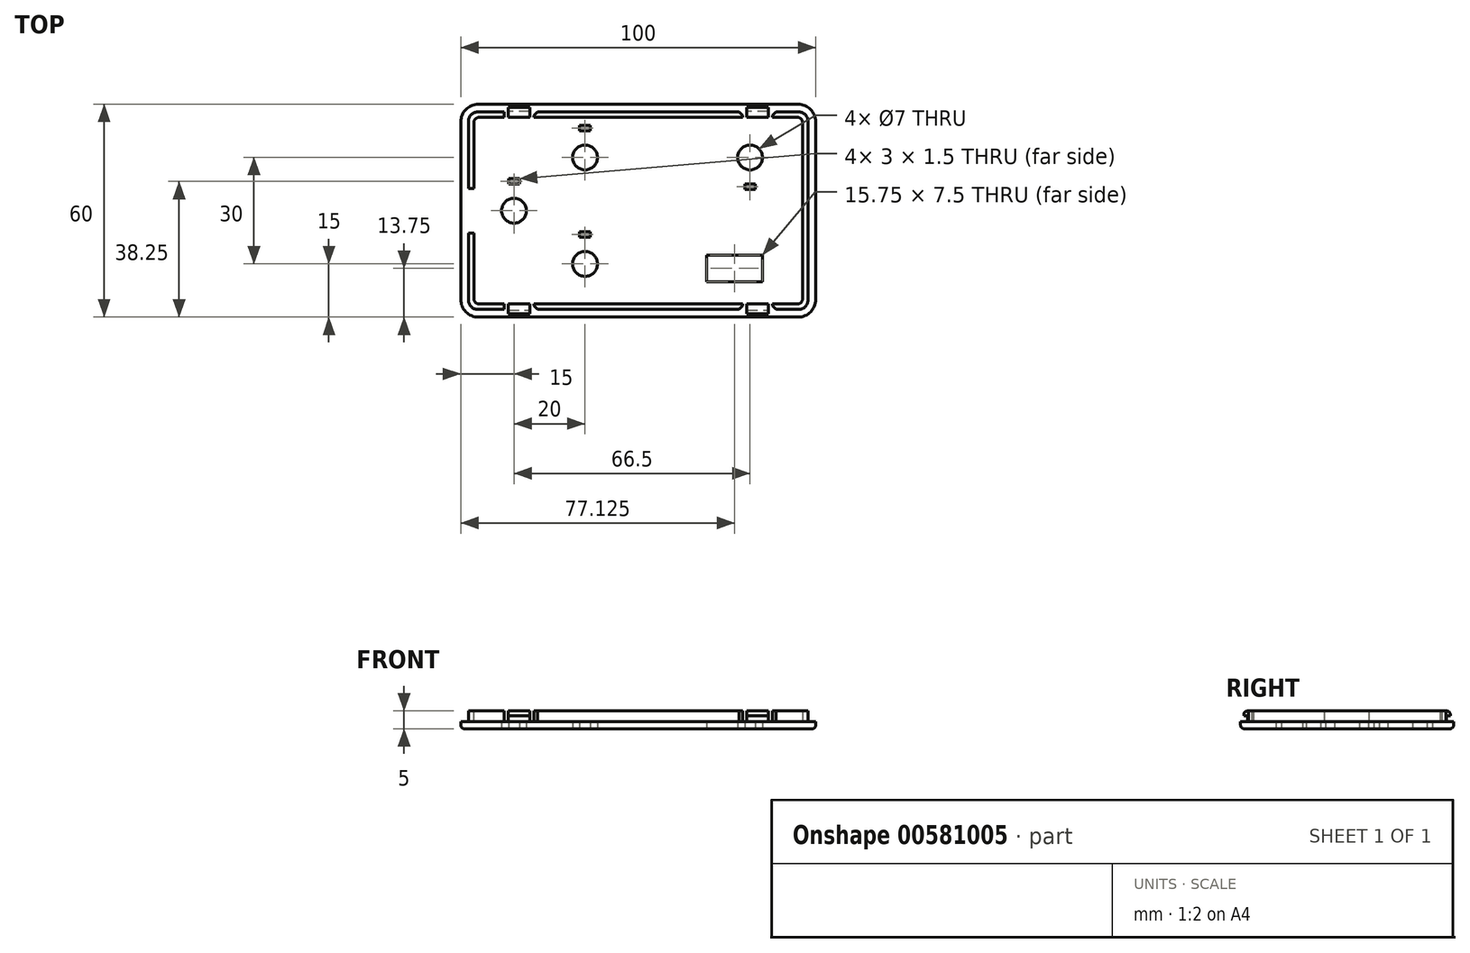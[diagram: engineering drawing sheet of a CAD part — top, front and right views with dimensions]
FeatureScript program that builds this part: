
annotation { "Feature Type Name" : "Feature", "Feature Type Description" : "" }
export const myFeature = defineFeature(function(context is Context, id is Id, definition is map)
    precondition{}
    {
        {
            var Q0;
            Q0=qCreatedBy(makeId("Top.planeOp"),FACE);
            var sketch = newSketch(context, id + "F0", { "sketchPlane" : qUnion([Q0])});
            skLineSegment(sketch, "E0.bottom", {"start": v(5, 0) * mm, "end": v(95, 0) * mm});
            skLineSegment(sketch, "E0.left", {"start": v(0, 5) * mm, "end": v(0, 30) * mm});
            skLineSegment(sketch, "E0.right", {"start": v(100, 5) * mm, "end": v(100, 30) * mm});
            skLineSegment(sketch, "E1.top", {"start": v(4.7, 2.2) * mm, "end": v(95.3, 2.2) * mm});
            skLineSegment(sketch, "E1.left", {"start": v(2.2, 30) * mm, "end": v(2.2, 4.7) * mm});
            skLineSegment(sketch, "E1.right", {"start": v(97.8, 30) * mm, "end": v(97.8, 4.7) * mm});
            skPoint(sketch, "E2.visualSharp", {"position": v(0, 0) * mm});
            skArc(sketch, "E2.filletArc", {"start": v(0, 5) * mm, "mid": v(1.46, 1.46) * mm, "end": v(5, 0) * mm});
            skPoint(sketch, "E3.visualSharp", {"position": v(100, 0) * mm});
            skArc(sketch, "E3.filletArc", {"start": v(95, 0) * mm, "mid": v(98.54, 1.46) * mm, "end": v(100, 5) * mm});
            skPoint(sketch, "E4.visualSharp", {"position": v(97.8, 2.2) * mm});
            skArc(sketch, "E4.filletArc", {"start": v(95.3, 2.2) * mm, "mid": v(97.07, 2.93) * mm, "end": v(97.8, 4.7) * mm});
            skPoint(sketch, "E5.visualSharp", {"position": v(2.2, 2.2) * mm});
            skArc(sketch, "E5.filletArc", {"start": v(2.2, 4.7) * mm, "mid": v(2.93, 2.93) * mm, "end": v(4.7, 2.2) * mm});
            skLineSegment(sketch, "E6.1", {"start": v(3.7, 30) * mm, "end": v(3.7, 5.2) * mm});
            skLineSegment(sketch, "E6.2", {"start": v(5.2, 3.7) * mm, "end": v(94.8, 3.7) * mm});
            skLineSegment(sketch, "E6.3", {"start": v(96.3, 30) * mm, "end": v(96.3, 5.2) * mm});
            skPoint(sketch, "E7.visualSharp", {"position": v(96.3, 3.7) * mm});
            skArc(sketch, "E7.filletArc", {"start": v(94.8, 3.7) * mm, "mid": v(95.86, 4.14) * mm, "end": v(96.3, 5.2) * mm});
            skPoint(sketch, "E8.visualSharp", {"position": v(3.7, 3.7) * mm});
            skArc(sketch, "E8.filletArc", {"start": v(3.7, 5.2) * mm, "mid": v(4.14, 4.14) * mm, "end": v(5.2, 3.7) * mm});
            skLineSegment(sketch, "E9", {"start": v(0, 30) * mm, "end": v(100, 30) * mm});
            skSolve(sketch);
        }
        {
            var Q0;
            Q0=qSketchRegion(id+"F0",true);
            var Q1;
            Q1=makeQuery(id+"F0.imprint","IMPRINT",FACE,{"disambiguationData":[TD([[makeQuery(id+"F0.imprint","IMPRINT",EDGE,{"derivedFrom":sQuery(id+"F0.wireOp",EDGE,"E6.0")}),-1.0]])]});
            var Q2;
            Q2=makeQuery(id+"F0.imprint","IMPRINT",FACE,{"disambiguationData":[TD([[makeQuery(id+"F0.imprint","IMPRINT",EDGE,{"derivedFrom":sQuery(id+"F0.wireOp",EDGE,"E1.bottom")}),-1.0]])]});
            extrude(context, id + "F1", {"entities" : qUnion([Q0, Q1, Q2]), "depth" : 2 * mm, "offsetDistance" : 25 * mm});
        }
        {
            var Q0;
            Q0=makeQuery(id+"F0.imprint","IMPRINT",FACE,{"disambiguationData":[TD([[makeQuery(id+"F0.imprint","IMPRINT",EDGE,{"derivedFrom":sQuery(id+"F0.wireOp",EDGE,"E1.top")}),1.0]])]});
            extrude(context, id + "F2", {"entities" : qUnion([Q0]), "operationType" : NewBodyOperationType.ADD, "depth" : 5 * mm, "offsetDistance" : 25 * mm});
        }
        {
            var Q0;
            Q0=makeQuery(id+"F2.opExtrude","CAP_FACE",FACE,{"disambiguationData":[OSD([sQuery(id+"F0.wireOp",EDGE,"E1.top"),sQuery(id+"F0.wireOp",EDGE,"E1.left"),sQuery(id+"F0.wireOp",EDGE,"E1.right"),sQuery(id+"F0.wireOp",EDGE,"E4.filletArc"),sQuery(id+"F0.wireOp",EDGE,"E5.filletArc"),sQuery(id+"F0.wireOp",EDGE,"E6.1"),sQuery(id+"F0.wireOp",EDGE,"E6.2"),sQuery(id+"F0.wireOp",EDGE,"E6.3"),sQuery(id+"F0.wireOp",EDGE,"E7.filletArc"),sQuery(id+"F0.wireOp",EDGE,"E8.filletArc"),sQuery(id+"F0.wireOp",EDGE,"E9")])],"isStart":false});
            var sketch = newSketch(context, id + "F3", { "sketchPlane" : qUnion([Q0])});
            skLineSegment(sketch, "E10.bottom", {"start": v(2.2, 30) * mm, "end": v(3.7, 30) * mm});
            skLineSegment(sketch, "E10.top", {"start": v(2.2, 23.7) * mm, "end": v(3.7, 23.7) * mm});
            skLineSegment(sketch, "E10.left", {"start": v(2.2, 30) * mm, "end": v(2.2, 23.7) * mm});
            skLineSegment(sketch, "E10.right", {"start": v(3.7, 30) * mm, "end": v(3.7, 23.7) * mm});
            skLineSegment(sketch, "E11.bottom", {"start": v(12.2, 3.7) * mm, "end": v(13.4, 3.7) * mm});
            skLineSegment(sketch, "E11.top", {"start": v(12.2, 2.2) * mm, "end": v(13.4, 2.2) * mm});
            skLineSegment(sketch, "E11.left", {"start": v(12.2, 3.7) * mm, "end": v(12.2, 2.2) * mm});
            skLineSegment(sketch, "E11.right", {"start": v(13.4, 3.7) * mm, "end": v(13.4, 2.2) * mm});
            skLineSegment(sketch, "E12.bottom", {"start": v(86.6, 3.7) * mm, "end": v(87.8, 3.7) * mm});
            skLineSegment(sketch, "E12.top", {"start": v(86.6, 2.2) * mm, "end": v(87.8, 2.2) * mm});
            skLineSegment(sketch, "E12.left", {"start": v(86.6, 3.7) * mm, "end": v(86.6, 2.2) * mm});
            skLineSegment(sketch, "E12.right", {"start": v(87.8, 3.7) * mm, "end": v(87.8, 2.2) * mm});
            skLineSegment(sketch, "E13.bottom", {"start": v(19.4, 3.7) * mm, "end": v(20.6, 3.7) * mm});
            skLineSegment(sketch, "E13.top", {"start": v(19.4, 2.2) * mm, "end": v(20.6, 2.2) * mm});
            skLineSegment(sketch, "E13.left", {"start": v(19.4, 3.7) * mm, "end": v(19.4, 2.2) * mm});
            skLineSegment(sketch, "E13.right", {"start": v(20.6, 3.7) * mm, "end": v(20.6, 2.2) * mm});
            skLineSegment(sketch, "E14.bottom", {"start": v(80.6, 3.7) * mm, "end": v(79.4, 3.7) * mm});
            skLineSegment(sketch, "E14.top", {"start": v(80.6, 2.2) * mm, "end": v(79.4, 2.2) * mm});
            skLineSegment(sketch, "E14.left", {"start": v(80.6, 3.7) * mm, "end": v(80.6, 2.2) * mm});
            skLineSegment(sketch, "E14.right", {"start": v(79.4, 3.7) * mm, "end": v(79.4, 2.2) * mm});
            skSolve(sketch);
        }
        {
            var Q0;
            Q0=makeQuery(id+"F3.imprint","IMPRINT",FACE,{"disambiguationData":[TD([[makeQuery(id+"F3.imprint","IMPRINT",EDGE,{"derivedFrom":sQuery(id+"F3.wireOp",EDGE,"E10.bottom")}),-1.0]])]});
            var Q1;
            Q1=makeQuery(id+"F3.imprint","IMPRINT",FACE,{"disambiguationData":[TD([[makeQuery(id+"F3.imprint","IMPRINT",EDGE,{"derivedFrom":sQuery(id+"F3.wireOp",EDGE,"E11.bottom")}),-1.0]])]});
            var Q2;
            Q2=makeQuery(id+"F3.imprint","IMPRINT",FACE,{"disambiguationData":[TD([[makeQuery(id+"F3.imprint","IMPRINT",EDGE,{"derivedFrom":sQuery(id+"F3.wireOp",EDGE,"E13.bottom")}),-1.0]])]});
            var Q3;
            Q3=makeQuery(id+"F3.imprint","IMPRINT",FACE,{"disambiguationData":[TD([[makeQuery(id+"F3.imprint","IMPRINT",EDGE,{"derivedFrom":sQuery(id+"F3.wireOp",EDGE,"E14.bottom")}),-1.0]])]});
            var Q4;
            Q4=makeQuery(id+"F3.imprint","IMPRINT",FACE,{"disambiguationData":[TD([[makeQuery(id+"F3.imprint","IMPRINT",EDGE,{"derivedFrom":sQuery(id+"F3.wireOp",EDGE,"E12.bottom")}),-1.0]])]});
            extrude(context, id + "F4", {"entities" : qUnion([Q0, Q1, Q2, Q3, Q4]), "operationType" : NewBodyOperationType.REMOVE, "oppositeDirection" : true, "depth" : 3 * mm, "offsetDistance" : 25 * mm});
        }
        {
            var Q0;
            {var subQ0=sQuery(id+"F3.wireOp",EDGE,"E11.right");var subQ2=sQuery(id+"F0.wireOp",EDGE,"E1.top");Q0=makeQuery(id+"F4.boolean.opBoolean","SPLIT",FACE,{"disambiguationData":[TD([makeQuery(id+"F4.opExtrude","SWEPT_FACE",FACE,{"disambiguationData":[OSD([subQ0])]})])],"derivedFrom":makeQuery(id+"F2.opExtrude","SWEPT_FACE",FACE,{"disambiguationData":[OSD([subQ2])]})});}
            var Q1;
            {var subQ1=sQuery(id+"F0.wireOp",EDGE,"E1.top");var subQ3=sQuery(id+"F3.wireOp",EDGE,"E12.left");Q1=makeQuery(id+"F4.boolean.opBoolean","SPLIT",FACE,{"disambiguationData":[TD([makeQuery(id+"F4.opExtrude","SWEPT_FACE",FACE,{"disambiguationData":[OSD([subQ3])]})])],"derivedFrom":makeQuery(id+"F2.opExtrude","SWEPT_FACE",FACE,{"disambiguationData":[OSD([subQ1])]})});}
            extrude(context, id + "F5", {"entities" : qUnion([Q0, Q1]), "operationType" : NewBodyOperationType.ADD, "depth" : 0.2 * mm, "offsetDistance" : 25 * mm});
        }
        {
            var Q0;
            {var subQ0=sQuery(id+"F3.wireOp",EDGE,"E11.right");var subQ2=sQuery(id+"F0.wireOp",EDGE,"E1.top");Q0=makeQuery(id+"F5.opExtrude","CAP_FACE",FACE,{"disambiguationData":[OSD([subQ2]),TDD([makeQuery(id+"F4.boolean.opBoolean","SPLIT",FACE,{"disambiguationData":[TD([makeQuery(id+"F4.opExtrude","SWEPT_FACE",FACE,{"disambiguationData":[OSD([subQ0])]})])],"derivedFrom":makeQuery(id+"F2.opExtrude","SWEPT_FACE",FACE,{"disambiguationData":[OSD([subQ2])]})})])],"isStart":false});}
            var sketch = newSketch(context, id + "F6", { "sketchPlane" : qUnion([Q0])});
            skLineSegment(sketch, "E15.bottom", {"start": v(13.4, 5) * mm, "end": v(19.4, 5) * mm});
            skLineSegment(sketch, "E15.top", {"start": v(13.4, 3.7) * mm, "end": v(19.4, 3.7) * mm});
            skLineSegment(sketch, "E15.left", {"start": v(13.4, 5) * mm, "end": v(13.4, 3.7) * mm});
            skLineSegment(sketch, "E15.right", {"start": v(19.4, 5) * mm, "end": v(19.4, 3.7) * mm});
            skSolve(sketch);
        }
        {
            var Q0;
            {var subQ1=sQuery(id+"F0.wireOp",EDGE,"E1.top");var subQ3=sQuery(id+"F3.wireOp",EDGE,"E12.left");Q0=makeQuery(id+"F5.opExtrude","CAP_FACE",FACE,{"disambiguationData":[OSD([subQ1]),TDD([makeQuery(id+"F4.boolean.opBoolean","SPLIT",FACE,{"disambiguationData":[TD([makeQuery(id+"F4.opExtrude","SWEPT_FACE",FACE,{"disambiguationData":[OSD([subQ3])]})])],"derivedFrom":makeQuery(id+"F2.opExtrude","SWEPT_FACE",FACE,{"disambiguationData":[OSD([subQ1])]})})])],"isStart":false});}
            var sketch = newSketch(context, id + "F7", { "sketchPlane" : qUnion([Q0])});
            skLineSegment(sketch, "E16.bottom", {"start": v(80.6, 5) * mm, "end": v(86.6, 5) * mm});
            skLineSegment(sketch, "E16.top", {"start": v(80.6, 3.7) * mm, "end": v(86.6, 3.7) * mm});
            skLineSegment(sketch, "E16.left", {"start": v(80.6, 5) * mm, "end": v(80.6, 3.7) * mm});
            skLineSegment(sketch, "E16.right", {"start": v(86.6, 5) * mm, "end": v(86.6, 3.7) * mm});
            skSolve(sketch);
        }
        {
            var Q0;
            Q0=makeQuery(id+"F6.imprint","IMPRINT",FACE,{"disambiguationData":[TD([[makeQuery(id+"F6.imprint","IMPRINT",EDGE,{"derivedFrom":sQuery(id+"F6.wireOp",EDGE,"E15.bottom")}),-1.0]])]});
            var Q1;
            Q1=makeQuery(id+"F7.imprint","IMPRINT",FACE,{"disambiguationData":[TD([[makeQuery(id+"F7.imprint","IMPRINT",EDGE,{"derivedFrom":sQuery(id+"F7.wireOp",EDGE,"E16.bottom")}),-1.0]])]});
            extrude(context, id + "F8", {"entities" : qUnion([Q0, Q1]), "operationType" : NewBodyOperationType.ADD, "depth" : 1.1 * mm, "offsetDistance" : 25 * mm});
        }
        {
            var Q0;
            Q0=makeQuery(id+"F8.opExtrude","CAP_EDGE",EDGE,{"disambiguationData":[OSD([sQuery(id+"F6.wireOp",EDGE,"E15.bottom")])],"isStart":false});
            var Q1;
            Q1=makeQuery(id+"F8.opExtrude","CAP_EDGE",EDGE,{"disambiguationData":[OSD([sQuery(id+"F7.wireOp",EDGE,"E16.bottom")])],"isStart":false});
            fillet(context, id + "F9", {"entities" : qUnion([Q0, Q1]), "radius" : 1 * mm, "tangentPropagation" : true, "allowEdgeOverflow" : false});
        }
        {
            var Q0;
            Q0=makeQuery(id+"F4.boolean.opBoolean","COPY",EDGE,{"derivedFrom":makeQuery(id+"F4.opExtrude","SWEPT_EDGE",EDGE,{"disambiguationData":[OSD([sQuery(id+"F0.wireOp",EDGE,"E1.top"),sQuery(id+"F3.wireOp",EDGE,"E13.top"),sQuery(id+"F3.wireOp",EDGE,"E13.right")])]})});
            var Q1;
            Q1=makeQuery(id+"F4.boolean.opBoolean","COPY",EDGE,{"derivedFrom":makeQuery(id+"F4.opExtrude","SWEPT_EDGE",EDGE,{"disambiguationData":[OSD([sQuery(id+"F0.wireOp",EDGE,"E1.top"),sQuery(id+"F3.wireOp",EDGE,"E11.top"),sQuery(id+"F3.wireOp",EDGE,"E11.left")])]})});
            var Q2;
            Q2=makeQuery(id+"F4.boolean.opBoolean","COPY",EDGE,{"derivedFrom":makeQuery(id+"F4.opExtrude","SWEPT_EDGE",EDGE,{"disambiguationData":[OSD([sQuery(id+"F0.wireOp",EDGE,"E1.top"),sQuery(id+"F3.wireOp",EDGE,"E14.top"),sQuery(id+"F3.wireOp",EDGE,"E14.right")])]})});
            var Q3;
            Q3=makeQuery(id+"F4.boolean.opBoolean","COPY",EDGE,{"derivedFrom":makeQuery(id+"F4.opExtrude","SWEPT_EDGE",EDGE,{"disambiguationData":[OSD([sQuery(id+"F0.wireOp",EDGE,"E1.top"),sQuery(id+"F3.wireOp",EDGE,"E12.top"),sQuery(id+"F3.wireOp",EDGE,"E12.right")])]})});
            var Q4;
            Q4=makeQuery(id+"F4.boolean.opBoolean","COPY",EDGE,{"derivedFrom":makeQuery(id+"F4.opExtrude","SWEPT_EDGE",EDGE,{"disambiguationData":[OSD([sQuery(id+"F0.wireOp",EDGE,"E1.left"),sQuery(id+"F3.wireOp",EDGE,"E10.top"),sQuery(id+"F3.wireOp",EDGE,"E10.left")])]})});
            chamfer(context, id + "F10", {"entities" : qUnion([Q0, Q1, Q2, Q3, Q4]), "width" : 1 * mm, "tangentPropagation" : true});
        }
        {
            var Q0;
            Q0=makeQuery(id+"F1.opExtrude","CAP_EDGE",EDGE,{"disambiguationData":[OSD([sQuery(id+"F0.wireOp",EDGE,"E0.bottom")])],"isStart":true});
            fillet(context, id + "F11", {"entities" : qUnion([Q0]), "radius" : 1 * mm, "tangentPropagation" : true, "allowEdgeOverflow" : false});
        }
        {
            var Q0;
            Q0=makeQuery(id+"F1.opExtrude","SWEPT_BODY",BODY,{"disambiguationData":[OSD([sQuery(id+"F0.wireOp",EDGE,"E0.bottom"),sQuery(id+"F0.wireOp",EDGE,"E0.left"),sQuery(id+"F0.wireOp",EDGE,"E0.right"),sQuery(id+"F0.wireOp",EDGE,"E2.filletArc"),sQuery(id+"F0.wireOp",EDGE,"E3.filletArc"),sQuery(id+"F0.wireOp",EDGE,"E9")])]});
            var Q1;
            {var subQ0=sQuery(id+"F0.wireOp",EDGE,"E0.left");var subQ1=sQuery(id+"F0.wireOp",EDGE,"E9");Q1=makeQuery(id+"FwHGnBZO1ZIo1Mn_1.boolean.opBoolean","SPLIT",FACE,{"disambiguationData":[TD([makeQuery(id+"F1.opExtrude","SWEPT_FACE",FACE,{"disambiguationData":[OSD([subQ0])]})])],"derivedFrom":makeQuery(id+"F2.boolean.opBoolean","MERGE",FACE,{"derivedFrom":[makeQuery(id+"F1.opExtrude","SWEPT_FACE",FACE,{"disambiguationData":[OSD([subQ1])]}),makeQuery(id+"F2.opExtrude","SWEPT_FACE",FACE,{"disambiguationData":[OSD([subQ1]),TDD([makeQuery(id+"F0.imprint","IMPRINT",EDGE,{"disambiguationData":[TD([[makeQuery(id+"F0.imprint","INTERSECT",VERTEX,{"derivedFrom":[sQuery(id+"F0.wireOp",EDGE,"E1.left"),subQ1]}),-1.0]])],"derivedFrom":subQ1})])]}),makeQuery(id+"F2.opExtrude","SWEPT_FACE",FACE,{"disambiguationData":[OSD([subQ1]),TDD([makeQuery(id+"F0.imprint","IMPRINT",EDGE,{"disambiguationData":[TD([[makeQuery(id+"F0.imprint","INTERSECT",VERTEX,{"derivedFrom":[sQuery(id+"F0.wireOp",EDGE,"E1.right"),subQ1]}),1.0]])],"derivedFrom":subQ1})])]})]})});}
            mirror(context, id + "F12", {"operationType" : NewBodyOperationType.ADD, "entities" : qUnion([Q0]), "mirrorPlane" : qUnion([Q1])});
        }
        {
            var Q0;
            Q0=qCreatedBy(makeId("Top.planeOp"),FACE);
            var sketch = newSketch(context, id + "F13", { "sketchPlane" : qUnion([Q0])});
            skCircle(sketch, "E17", {"center": v(15, 30) * mm, "radius": 3.5 * mm});
            skCircle(sketch, "E18", {"center": v(35, 15) * mm, "radius": 3.5 * mm});
            skCircle(sketch, "E19", {"center": v(35, 45) * mm, "radius": 3.5 * mm});
            skCircle(sketch, "E20", {"center": v(81.5, 45) * mm, "radius": 3.5 * mm});
            skLineSegment(sketch, "E21.bottom", {"start": v(13.5, 37.5) * mm, "end": v(16.5, 37.5) * mm});
            skLineSegment(sketch, "E21.top", {"start": v(13.5, 39) * mm, "end": v(16.5, 39) * mm});
            skLineSegment(sketch, "E21.left", {"start": v(13.5, 37.5) * mm, "end": v(13.5, 39) * mm});
            skLineSegment(sketch, "E21.right", {"start": v(16.5, 37.5) * mm, "end": v(16.5, 39) * mm});
            skPoint(sketch, "E22.startSnap0", {"position": v(15, 37.5) * mm});
            skLineSegment(sketch, "E23", {"start": v(15, 37.5) * mm, "end": v(15, 30) * mm});
            skLineSegment(sketch, "E24.bottom", {"start": v(33.5, 22.5) * mm, "end": v(36.5, 22.5) * mm});
            skLineSegment(sketch, "E24.top", {"start": v(33.5, 24) * mm, "end": v(36.5, 24) * mm});
            skLineSegment(sketch, "E24.left", {"start": v(33.5, 22.5) * mm, "end": v(33.5, 24) * mm});
            skLineSegment(sketch, "E24.right", {"start": v(36.5, 22.5) * mm, "end": v(36.5, 24) * mm});
            skPoint(sketch, "E25.startSnap0", {"position": v(35, 22.5) * mm});
            skLineSegment(sketch, "E26", {"start": v(35, 22.5) * mm, "end": v(35, 15) * mm});
            skLineSegment(sketch, "E27.bottom", {"start": v(33.5, 52.5) * mm, "end": v(36.5, 52.5) * mm});
            skLineSegment(sketch, "E27.top", {"start": v(33.5, 54) * mm, "end": v(36.5, 54) * mm});
            skLineSegment(sketch, "E27.left", {"start": v(33.5, 52.5) * mm, "end": v(33.5, 54) * mm});
            skLineSegment(sketch, "E27.right", {"start": v(36.5, 52.5) * mm, "end": v(36.5, 54) * mm});
            skPoint(sketch, "E28.startSnap0", {"position": v(35, 52.5) * mm});
            skLineSegment(sketch, "E29", {"start": v(35, 52.5) * mm, "end": v(35, 45) * mm});
            skLineSegment(sketch, "E30.bottom", {"start": v(80, 36) * mm, "end": v(83, 36) * mm});
            skLineSegment(sketch, "E30.top", {"start": v(80, 37.5) * mm, "end": v(83, 37.5) * mm});
            skLineSegment(sketch, "E30.left", {"start": v(80, 36) * mm, "end": v(80, 37.5) * mm});
            skLineSegment(sketch, "E30.right", {"start": v(83, 36) * mm, "end": v(83, 37.5) * mm});
            skPoint(sketch, "E31.startSnap0", {"position": v(81.5, 36) * mm});
            skLineSegment(sketch, "E32.bottom", {"start": v(69.25, 10) * mm, "end": v(85, 10) * mm});
            skLineSegment(sketch, "E32.top", {"start": v(69.25, 17.5) * mm, "end": v(85, 17.5) * mm});
            skLineSegment(sketch, "E32.left", {"start": v(69.25, 10) * mm, "end": v(69.25, 17.5) * mm});
            skLineSegment(sketch, "E32.right", {"start": v(85, 10) * mm, "end": v(85, 17.5) * mm});
            skSolve(sketch);
        }
        {
            var Q0;
            Q0=makeQuery(id+"F13.imprint","IMPRINT",FACE,{"disambiguationData":[TD([[makeQuery(id+"F13.imprint","IMPRINT",EDGE,{"derivedFrom":sQuery(id+"F13.wireOp",EDGE,"E17")}),1.0]])]});
            var Q1;
            Q1=makeQuery(id+"F13.imprint","IMPRINT",FACE,{"disambiguationData":[TD([[makeQuery(id+"F13.imprint","IMPRINT",EDGE,{"derivedFrom":sQuery(id+"F13.wireOp",EDGE,"E21.top")}),-1.0]])]});
            var Q2;
            Q2=makeQuery(id+"F13.imprint","IMPRINT",FACE,{"disambiguationData":[TD([[makeQuery(id+"F13.imprint","IMPRINT",EDGE,{"derivedFrom":sQuery(id+"F13.wireOp",EDGE,"E19")}),1.0]])]});
            var Q3;
            Q3=makeQuery(id+"F13.imprint","IMPRINT",FACE,{"disambiguationData":[TD([[makeQuery(id+"F13.imprint","IMPRINT",EDGE,{"derivedFrom":sQuery(id+"F13.wireOp",EDGE,"E27.top")}),-1.0]])]});
            var Q4;
            Q4=makeQuery(id+"F13.imprint","IMPRINT",FACE,{"disambiguationData":[TD([[makeQuery(id+"F13.imprint","IMPRINT",EDGE,{"derivedFrom":sQuery(id+"F13.wireOp",EDGE,"E18")}),1.0]])]});
            var Q5;
            Q5=makeQuery(id+"F13.imprint","IMPRINT",FACE,{"disambiguationData":[TD([[makeQuery(id+"F13.imprint","IMPRINT",EDGE,{"derivedFrom":sQuery(id+"F13.wireOp",EDGE,"E32.bottom")}),1.0]])]});
            var Q6;
            Q6=makeQuery(id+"F13.imprint","IMPRINT",FACE,{"disambiguationData":[TD([[makeQuery(id+"F13.imprint","IMPRINT",EDGE,{"derivedFrom":sQuery(id+"F13.wireOp",EDGE,"E20")}),1.0]])]});
            var Q7;
            Q7=makeQuery(id+"F13.imprint","IMPRINT",FACE,{"disambiguationData":[TD([[makeQuery(id+"F13.imprint","IMPRINT",EDGE,{"derivedFrom":sQuery(id+"F13.wireOp",EDGE,"E30.top")}),-1.0]])]});
            var Q8;
            Q8=makeQuery(id+"F13.imprint","IMPRINT",FACE,{"disambiguationData":[TD([[makeQuery(id+"F13.imprint","IMPRINT",EDGE,{"derivedFrom":sQuery(id+"F13.wireOp",EDGE,"E24.top")}),-1.0]])]});
            extrude(context, id + "F14", {"entities" : qUnion([Q0, Q1, Q2, Q3, Q4, Q5, Q6, Q7, Q8]), "operationType" : NewBodyOperationType.REMOVE, "endBound" : BoundingType.UP_TO_NEXT, "depth" : 25 * mm, "offsetDistance" : 25 * mm});
        }
    });
